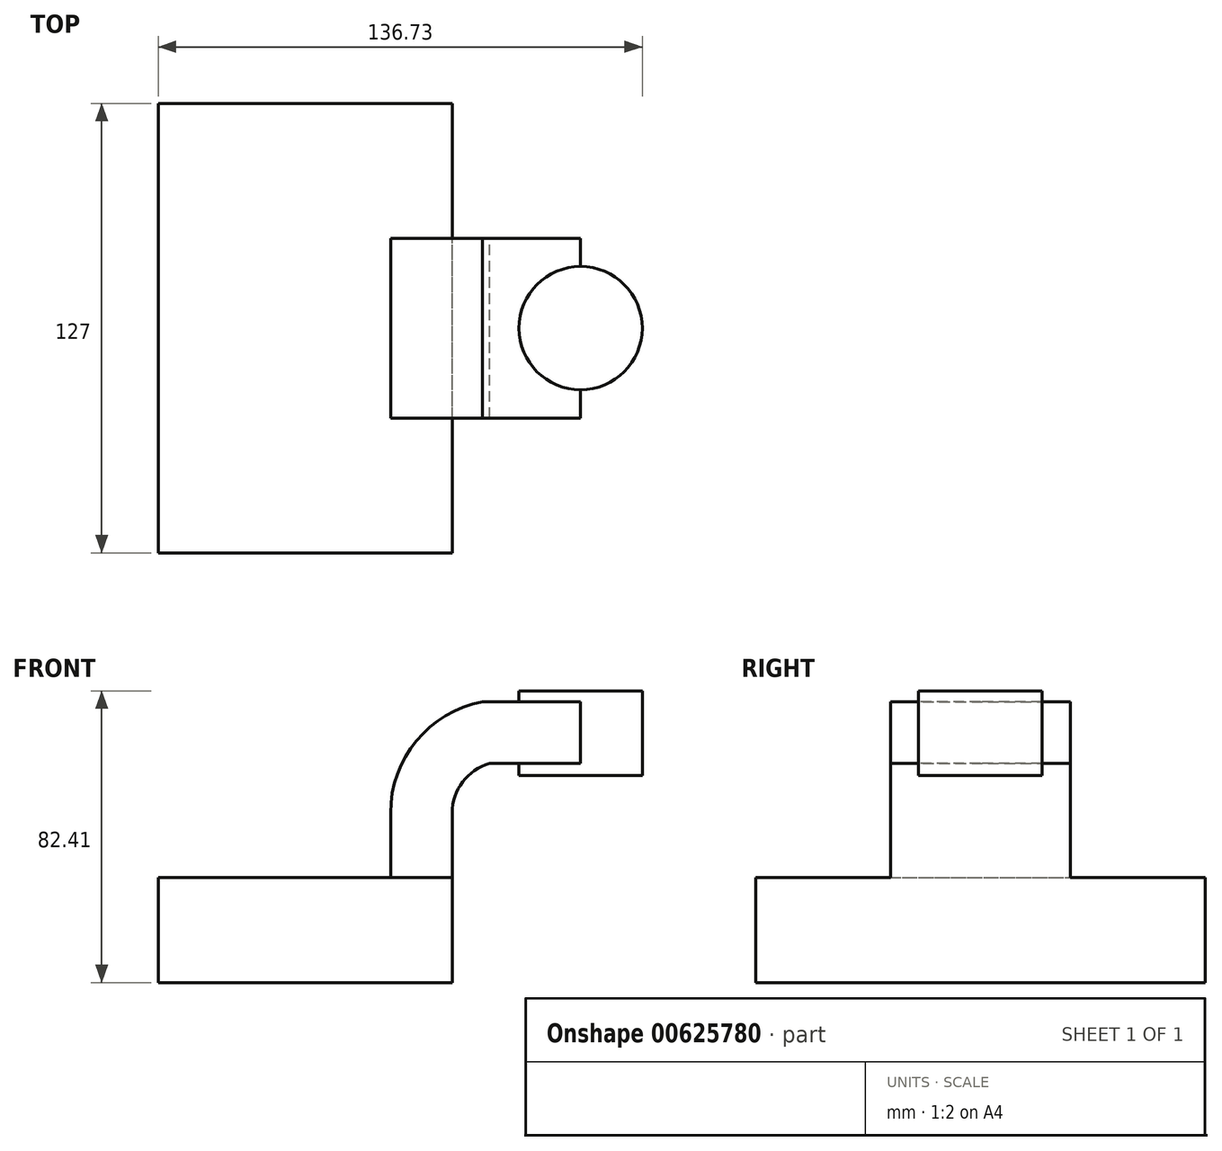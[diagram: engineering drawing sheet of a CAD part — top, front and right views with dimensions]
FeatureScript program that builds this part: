
annotation { "Feature Type Name" : "Feature", "Feature Type Description" : "" }
export const myFeature = defineFeature(function(context is Context, id is Id, definition is map)
    precondition{}
    {
        {
            var Q0;
            Q0=qCreatedBy(makeId("Front.planeOp"),FACE);
            var sketch = newSketch(context, id + "F0", { "sketchPlane" : qUnion([Q0])});
            skLineSegment(sketch, "E0.bottom", {"start": v(-24.3, -20.02) * mm, "end": v(58.72, -20.02) * mm});
            skLineSegment(sketch, "E0.top", {"start": v(-24.3, 9.66) * mm, "end": v(58.72, 9.66) * mm});
            skLineSegment(sketch, "E0.left", {"start": v(-24.3, -20.02) * mm, "end": v(-24.3, 9.66) * mm});
            skLineSegment(sketch, "E0.right", {"start": v(58.72, -20.02) * mm, "end": v(58.72, 9.66) * mm});
            skPoint(sketch, "E0.middle", {"position": v(17.2, -5.18) * mm});
            skLineSegment(sketch, "E1.bottom", {"start": v(77.59, 38.48) * mm, "end": v(112.42, 38.48) * mm});
            skLineSegment(sketch, "E1.top", {"start": v(77.59, 62.39) * mm, "end": v(112.42, 62.39) * mm});
            skLineSegment(sketch, "E1.left", {"start": v(77.59, 38.48) * mm, "end": v(77.59, 62.39) * mm});
            skLineSegment(sketch, "E1.right", {"start": v(112.42, 38.48) * mm, "end": v(112.42, 62.39) * mm});
            skPoint(sketch, "E1.middle", {"position": v(95, 50.44) * mm});
            skLineSegment(sketch, "E2", {"start": v(58.72, 9.66) * mm, "end": v(58.72, 27.94) * mm});
            skArc(sketch, "E3", {"start": v(58.72, 27.94) * mm, "mid": v(61.65, 36.68) * mm, "end": v(69.25, 41.9) * mm});
            skLineSegment(sketch, "E4", {"start": v(69.25, 41.9) * mm, "end": v(95, 41.9) * mm});
            skLineSegment(sketch, "E5", {"start": v(95, 38.48) * mm, "end": v(95, 62.39) * mm});
            skLineSegment(sketch, "E6.0", {"start": v(67.28, 59.32) * mm, "end": v(95, 59.32) * mm});
            skArc(sketch, "E6.1", {"start": v(41.3, 27.94) * mm, "mid": v(48.64, 48.3) * mm, "end": v(67.28, 59.32) * mm});
            skLineSegment(sketch, "E6.2", {"start": v(41.3, 9.58) * mm, "end": v(41.3, 27.94) * mm});
            skFitSpline(sketch, "E7", {"points": [v(-24.3, 9.66) * mm, v(67.28, 59.32) * mm], "startDerivative": vector(0, 111.08) * mm, "endDerivative": vector(123.75, -0.1) * mm});
            skSolve(sketch);
        }
        {
            var Q0;
            Q0=makeQuery(id+"F0.imprint","IMPRINT",FACE,{"disambiguationData":[TD([[makeQuery(id+"F0.imprint","IMPRINT",EDGE,{"derivedFrom":sQuery(id+"F0.wireOp",EDGE,"E0.bottom")}),1.0]])]});
            extrude(context, id + "F1", {"entities" : qUnion([Q0]), "endBound" : BoundingType.SYMMETRIC, "depth" : 127 * mm, "offsetDistance" : 25.4 * mm});
        }
        {
            var Q0;
            {var subQ1=sQuery(id+"F0.wireOp",EDGE,"E2");Q0=makeQuery(id+"F0.imprint","IMPRINT",FACE,{"disambiguationData":[TD([[makeQuery(id+"F0.imprint","IMPRINT",EDGE,{"derivedFrom":subQ1}),1.0]])]});}
            var Q1;
            {var subQ0=sQuery(id+"F0.wireOp",EDGE,"E4");var subQ1=sQuery(id+"F0.wireOp",EDGE,"E1.left");var subQ2=makeQuery(id+"F0.imprint","INTERSECT",VERTEX,{"derivedFrom":[subQ1,subQ0]});Q1=makeQuery(id+"F0.imprint","IMPRINT",FACE,{"disambiguationData":[TD([[makeQuery(id+"F0.imprint","IMPRINT",EDGE,{"disambiguationData":[TD([[subQ2,-1.0]])],"derivedFrom":subQ1}),-1.0]])]});}
            extrude(context, id + "F2", {"entities" : qUnion([Q0, Q1]), "operationType" : NewBodyOperationType.ADD, "endBound" : BoundingType.SYMMETRIC, "depth" : 50.8 * mm, "offsetDistance" : 25.4 * mm});
        }
        {
            var Q0;
            {var subQ4=sQuery(id+"F0.wireOp",EDGE,"E6.1");Q0=makeQuery(id+"F0.imprint","IMPRINT",FACE,{"disambiguationData":[TD([[makeQuery(id+"F0.imprint","IMPRINT",EDGE,{"derivedFrom":subQ4}),1.0]])]});}
            extrude(context, id + "F3", {"entities" : qUnion([Q0]), "operationType" : NewBodyOperationType.ADD, "endBound" : BoundingType.SYMMETRIC, "depth" : 15.88 * mm, "offsetDistance" : 25.4 * mm});
        }
        {
            var Q0;
            {var subQ4=sQuery(id+"F0.wireOp",EDGE,"E1.right");Q0=makeQuery(id+"F0.imprint","IMPRINT",FACE,{"disambiguationData":[TD([[makeQuery(id+"F0.imprint","IMPRINT",EDGE,{"derivedFrom":subQ4}),1.0]])]});}
            var Q1;
            Q1=sQuery(id+"F0.wireOp",EDGE,"E5");
            revolve(context, id + "F4", {"operationType" : NewBodyOperationType.ADD, "entities" : qUnion([Q0]), "axis" : qUnion([Q1]), "revolveType" : RevolveType.FULL});
        }
    });
